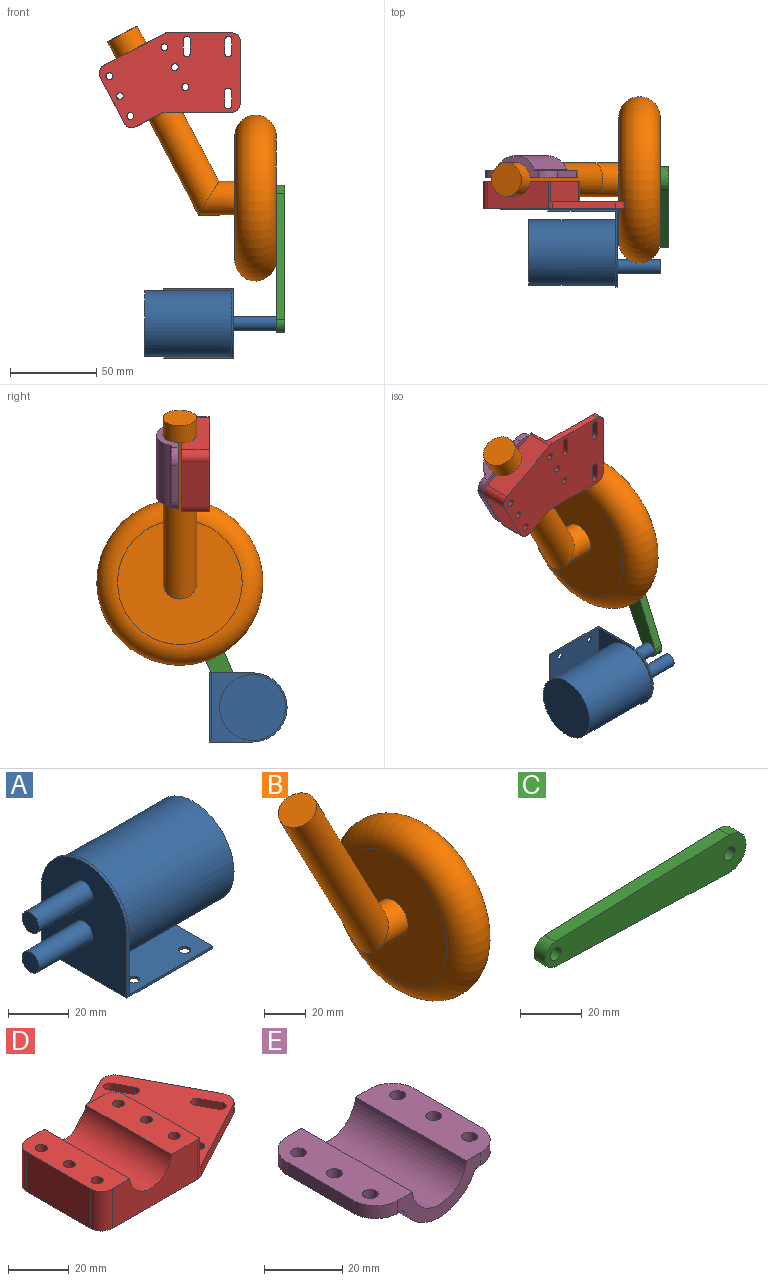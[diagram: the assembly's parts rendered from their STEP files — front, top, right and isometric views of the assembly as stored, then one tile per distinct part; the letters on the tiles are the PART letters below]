
ASSEMBLY  parts=5 mates=6
PART A: 18 faces, bbox 76x40x45 mm
  f0: plane 45x40mm, normal (-1,0,0), area 1527.8mm2, adj f1,f5,f6,f7,f12,f14
  f1: plane 40x40mm, normal (0,0,-1), area 1549.7mm2, adj f0,f2,f5,f6,f8,f9,f10,f11
  f2: plane 40x1mm, normal (1,0,0), area 40mm2, adj f1,f3,f5,f6
  f3: plane 40x39mm, normal (0,0,1), area 1509.7mm2, adj f2,f4,f5,f6,f8,f9,f10,f11
  f4: plane 44x40mm, normal (1,0,0), area 454.2mm2, adj f3,f5,f6,f7,f16
  f5: plane 40x25mm, normal (0,-1,0), area 64mm2, adj f0,f1,f2,f3,f4,f7
  f6: plane 40x25mm, normal (0,1,0), area 64mm2, adj f0,f1,f2,f3,f4,f7
  f7: cylinder r=20mm len=40mm, axis (1,0,0), area 62.8mm2, adj f0,f4,f5,f6
  f8: cylinder r=2mm len=4mm, axis (0,0,1), area 12.6mm2, adj f1,f3
  f9: cylinder r=2mm len=4mm, axis (0,0,1), area 12.6mm2, adj f1,f3
  f10: cylinder r=2mm len=4mm, axis (0,0,1), area 12.6mm2, adj f1,f3
  f11: cylinder r=2mm len=4mm, axis (0,0,1), area 12.6mm2, adj f1,f3
  f12: cylinder r=4mm len=25mm, axis (1,0,0), area 628.3mm2, adj f0,f13
  f13: plane 8x8mm, normal (-1,0,0), area 50.3mm2, adj f12
  f14: cylinder r=4mm len=25mm, axis (1,0,0), area 628.3mm2, adj f0,f15
  f15: plane 8x8mm, normal (-1,0,0), area 50.3mm2, adj f14
  f16: cylinder r=19mm len=50mm, axis (-1,0,0), area 5969mm2, adj f4,f17
  f17: plane 38x38mm, normal (1,0,0), area 1134.1mm2, adj f16
PART B: 6 faces, bbox 97.6x103.9x151.5 mm
  f0: plane 19.5x17.26mm, normal (-0.47,0,0.88), area 298.6mm2, adj f1
  f1: cylinder r=9.75mm len=109.29mm, axis (-0.47,0,0.88), area 6576.7mm2, adj f0,f2
  f2: cylinder r=9.75mm len=20.89mm, axis (-1,0,0), area 918.9mm2, adj f1,f3
  f3: plane 72x72mm, normal (-1,0,0), area 3772.9mm2, adj f2,f5
  f4: plane 72x72mm, normal (1,0,0), area 4071.5mm2, adj f5
  f5: torus R=36mm, axis (-1,0,0), area 10336.9mm2, adj f3,f4
PART C: 8 faces, bbox 92.5x5x15 mm
  f0: plane 79.92x5mm, normal (-0.03,0,-1), area 399.8mm2, adj f1,f5,f6,f7
  f1: cylinder r=7.5mm len=15mm, axis (0,1,0), area 120.2mm2, adj f0,f2,f6,f7
  f2: plane 79.92x5mm, normal (-0.03,0,1), area 399.8mm2, adj f1,f5,f6,f7
  f3: cylinder r=2.5mm len=5mm, axis (0,1,0), area 78.5mm2, adj f6,f7
  f4: cylinder r=2.5mm len=5mm, axis (0,1,0), area 78.5mm2, adj f6,f7
  f5: cylinder r=5mm len=10mm, axis (0,1,0), area 77mm2, adj f0,f2,f6,f7
  f6: plane 92.5x15mm, normal (0,-1,0), area 1088.8mm2, adj f0,f1,f2,f3,f4,f5
  f7: plane 92.5x15mm, normal (0,1,0), area 1088.8mm2, adj f0,f1,f2,f3,f4,f5
PART D: 37 faces, bbox 82x58.9x16 mm
  f0: plane 60.01x58.78mm, normal (0,0,1), area 1403.9mm2, adj f2,f3,f9,f16,f17,f18,f19,f20
  f1: plane 82.01x58.94mm, normal (0,0,-1), area 3152.4mm2, adj f2,f7,f8,f9,f10,f11,f12,f13
  f2: plane 32.26x17.15mm, normal (0.47,-0.88,0), area 146.1mm2, adj f0,f1,f30,f36
  f3: plane 34.84x12mm, normal (1,0,0), area 418.1mm2, adj f0,f4,f30,f32
  f4: plane 40x13.25mm, normal (0,0,1), area 486.9mm2, adj f3,f5,f8,f9,f10,f11,f12,f30
  f5: cylinder r=9.8mm len=40mm, axis (0,1,0), area 1151.4mm2, adj f4,f6,f8,f9
  f6: plane 40x13.25mm, normal (0,0,1), area 481.6mm2, adj f5,f7,f8,f9,f13,f14,f15,f31
  f7: plane 30x16mm, normal (-1,0,0), area 480mm2, adj f1,f6,f31,f33
  f8: plane 39.75x16mm, normal (0,-1,0), area 504.8mm2, adj f1,f4,f5,f6,f30,f33
  f9: plane 36x16mm, normal (0,1,0), area 368.7mm2, adj f0,f1,f4,f5,f6,f29,f31,f32
  f10: cylinder r=2mm len=16mm, axis (0,0,-1), area 201.1mm2, adj f1,f4
  f11: cylinder r=2mm len=16mm, axis (0,0,-1), area 201.1mm2, adj f1,f4
  f12: cylinder r=2mm len=16mm, axis (0,0,-1), area 201.1mm2, adj f1,f4
  f13: cylinder r=2mm len=16mm, axis (0,0,-1), area 201.1mm2, adj f1,f6
  f14: cylinder r=2mm len=16mm, axis (0,0,-1), area 201.1mm2, adj f1,f6
  f15: cylinder r=2mm len=16mm, axis (0,0,-1), area 201.1mm2, adj f1,f6
  f16: cylinder r=2mm len=4mm, axis (0,0,-1), area 25.1mm2, adj f0,f1,f17,f19
  f17: plane 7.06x4mm, normal (0.88,0.47,0), area 32mm2, adj f0,f1,f16,f18
  f18: cylinder r=2mm len=4mm, axis (0,0,-1), area 25.1mm2, adj f0,f1,f17,f19
  f19: plane 7.06x4mm, normal (-0.88,-0.47,0), area 32mm2, adj f0,f1,f16,f18
  f20: cylinder r=2mm len=4mm, axis (0,0,-1), area 25.1mm2, adj f0,f1,f21,f23
  f21: plane 7.06x4mm, normal (-0.88,-0.47,0), area 32mm2, adj f0,f1,f20,f22
  f22: cylinder r=2mm len=4mm, axis (0,0,-1), area 25.1mm2, adj f0,f1,f21,f23
  f23: plane 7.06x4mm, normal (0.88,0.47,0), area 32mm2, adj f0,f1,f20,f22
  f24: plane 7.06x4mm, normal (-0.88,-0.47,0), area 32mm2, adj f0,f1,f25,f27
  f25: cylinder r=2mm len=4mm, axis (0,0,-1), area 25.1mm2, adj f0,f1,f24,f26
  f26: plane 7.06x4mm, normal (0.88,0.47,0), area 32mm2, adj f0,f1,f25,f27
  f27: cylinder r=2mm len=4mm, axis (0,0,-1), area 25.1mm2, adj f0,f1,f24,f26
  f28: plane 33.41x17.77mm, normal (-0.47,0.88,0), area 151.4mm2, adj f0,f1,f29,f35
  f29: cylinder r=5mm len=4mm, axis (0,0,1), area 9.8mm2, adj f0,f1,f9,f28
  f30: cylinder r=5mm len=16mm, axis (0,0,-1), area 24.9mm2, adj f0,f1,f2,f3,f4,f8
  f31: cylinder r=5mm len=16mm, axis (0,0,-1), area 125.7mm2, adj f1,f6,f7,f9
  f32: cylinder r=5mm len=12mm, axis (0,0,1), area 94.2mm2, adj f0,f3,f4,f9
  f33: cylinder r=5mm len=16mm, axis (0,0,1), area 125.7mm2, adj f1,f6,f7,f8
  f34: plane 31.79x16.9mm, normal (0.88,0.47,0), area 144mm2, adj f0,f1,f35,f36
  f35: cylinder r=5mm len=6.76mm, axis (0,0,-1), area 31.4mm2, adj f0,f1,f28,f34
  f36: cylinder r=5mm len=6.76mm, axis (0,0,1), area 31.4mm2, adj f0,f1,f2,f34
PART E: 22 faces, bbox 46x40x12.8 mm
  f0: plane 40x13.25mm, normal (0,0,1), area 464.9mm2, adj f1,f7,f8,f9,f13,f14,f15,f17
  f1: plane 24x4mm, normal (-1,0,0), area 96mm2, adj f0,f2,f17,f19
  f2: plane 40x9.15mm, normal (0,0,-1), area 300.8mm2, adj f1,f8,f9,f13,f14,f15,f17,f19
  f3: cylinder r=13.8mm len=40mm, axis (0,1,0), area 1249.7mm2, adj f8,f9,f20,f21
  f4: plane 40x9.15mm, normal (0,0,-1), area 300.8mm2, adj f5,f8,f9,f10,f11,f12,f16,f18
  f5: plane 24x4mm, normal (1,0,0), area 96mm2, adj f4,f6,f16,f18
  f6: plane 40x13.25mm, normal (0,0,1), area 464.9mm2, adj f5,f7,f8,f9,f10,f11,f12,f16
  f7: cylinder r=9.8mm len=40mm, axis (0,1,0), area 1151.4mm2, adj f0,f6,f8,f9
  f8: plane 30x12.8mm, normal (0,-1,0), area 153.3mm2, adj f0,f2,f3,f4,f6,f7,f18,f19
  f9: plane 30x12.8mm, normal (0,1,0), area 153.3mm2, adj f0,f2,f3,f4,f6,f7,f16,f17
  f10: cylinder r=2mm len=4mm, axis (0,0,-1), area 50.3mm2, adj f4,f6
  f11: cylinder r=2mm len=4mm, axis (0,0,-1), area 50.3mm2, adj f4,f6
  f12: cylinder r=2mm len=4mm, axis (0,0,-1), area 50.3mm2, adj f4,f6
  f13: cylinder r=2mm len=4mm, axis (0,0,-1), area 50.3mm2, adj f0,f2
  f14: cylinder r=2mm len=4mm, axis (0,0,-1), area 50.3mm2, adj f0,f2
  f15: cylinder r=2mm len=4mm, axis (0,0,-1), area 50.3mm2, adj f0,f2
  f16: cylinder r=8mm len=8mm, axis (0,0,1), area 50.3mm2, adj f4,f5,f6,f9
  f17: cylinder r=8mm len=8mm, axis (0,0,-1), area 50.3mm2, adj f0,f1,f2,f9
  f18: cylinder r=8mm len=8mm, axis (0,0,-1), area 50.3mm2, adj f4,f5,f6,f8
  f19: cylinder r=8mm len=8mm, axis (0,0,1), area 50.3mm2, adj f0,f1,f2,f8
  f20: cylinder r=1.5mm len=40mm, axis (0,1,0), area 67.9mm2, adj f2,f3,f8,f9
  f21: cylinder r=1.5mm len=40mm, axis (0,1,0), area 67.9mm2, adj f3,f4,f8,f9
PLACE A rot(axis=(0,0.71,-0.71),180deg) t=(-7.66,-17.72,-79.49)mm
PLACE B t=(-6.66,-0.72,12.93)mm fixed
PLACE C rot(axis=(0.47,-0.47,0.74),106.7deg) t=(17.34,-0.72,12.93)mm
PLACE D rot(axis=(-0.94,-0.23,-0.23),93.3deg) t=(-68.23,-1.72,51.87)mm
PLACE E rot(axis=(0.17,0.7,-0.7),160.5deg) t=(-27.46,0.28,73.33)mm
MATE revolute D.f13 <-> E.f10  axis (0,1,0) through (-67.07,-1.72,60.4)mm
MATE revolute D.f12 <-> E.f14  axis (0,1,0) through (-47.32,-1.72,100.17)mm
MATE slider E.f3 <-> B.f1  axis (0.47,0,-0.88) through (-66.45,-0.72,98.02)mm
MATE cylindrical C.f3 <-> A.f14  axis (-1,0,0) through (17.34,-34.72,-59.49)mm
MATE planar A.f1 <-> D.f1  axis (0,1,0) through (-27.66,-17.72,-59.49)mm
MATE revolute B.f5 <-> C.f4  axis (1,0,0) through (17.34,-0.72,12.93)mm
